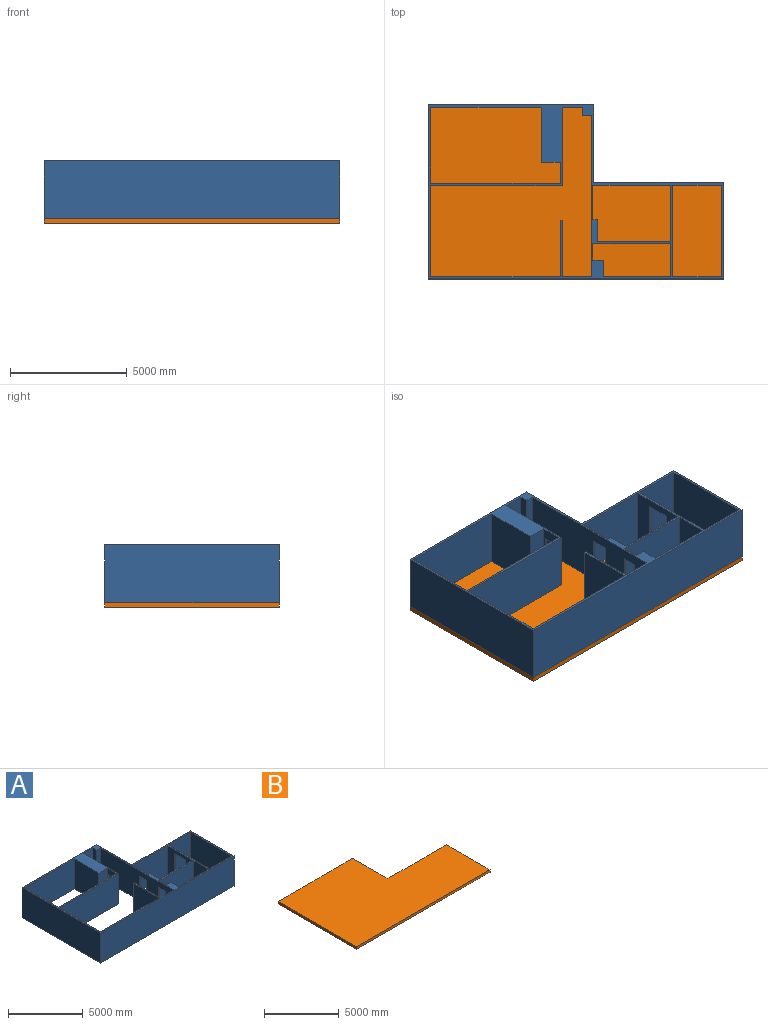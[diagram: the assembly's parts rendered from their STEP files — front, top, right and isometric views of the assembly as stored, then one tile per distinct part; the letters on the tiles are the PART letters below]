
ASSEMBLY  parts=2 mates=1
PART A: 54 faces, bbox 12650x7451.1x2470 mm
  f0: plane 12650x7451.1mm, normal (0,0,-1), area 8166293mm2, adj f1,f2,f3,f4,f5,f6,f7,f8
  f1: plane 2470x2420mm, normal (-1,0,0), area 3816000mm2, adj f0,f14,f15,f41,f48,f49,f50
  f2: plane 2470x1490mm, normal (1,0,0), area 2260300mm2, adj f0,f14,f35,f41,f45,f46,f47
  f3: plane 5630x2470mm, normal (0,-1,0), area 13906100mm2, adj f0,f4,f40,f41
  f4: plane 3351.1x2470mm, normal (1,0,0), area 6857217mm2, adj f0,f3,f5,f41,f51,f52,f53
  f5: plane 2470x890mm, normal (0,-1,0), area 2198300mm2, adj f0,f4,f6,f41
  f6: plane 2470x350mm, normal (-1,0,0), area 864500mm2, adj f0,f5,f7,f41
  f7: plane 2470x360mm, normal (0,-1,0), area 889200mm2, adj f0,f6,f8,f41
  f8: plane 6901.1x2470mm, normal (-1,0,0), area 14405717mm2, adj f0,f7,f9,f41,f42,f43,f44,f45
  f9: plane 2470x1250mm, normal (0,1,0), area 3087500mm2, adj f0,f8,f10,f41
  f10: plane 2470x2420mm, normal (1,0,0), area 5977400mm2, adj f0,f9,f11,f41
  f11: plane 2470x80mm, normal (0,1,0), area 197600mm2, adj f0,f10,f12,f41
  f12: plane 2470x2420mm, normal (-1,0,0), area 5977400mm2, adj f0,f11,f13,f41
  f13: plane 5550x2470mm, normal (0,1,0), area 13708500mm2, adj f0,f12,f40,f41
  f14: plane 3310x2470mm, normal (0,-1,0), area 8175700mm2, adj f0,f1,f2,f41
  f15: plane 3130x2470mm, normal (0,1,0), area 7731100mm2, adj f0,f1,f16,f41
  f16: plane 2470x930mm, normal (1,0,0), area 2297100mm2, adj f0,f15,f35,f41
  f17: plane 2470x901.1mm, normal (-1,0,0), area 805717mm2, adj f0,f18,f36,f41,f51,f52,f53
  f18: plane 5550x2470mm, normal (0,1,0), area 13708500mm2, adj f0,f17,f19,f41
  f19: plane 3251.1x2470mm, normal (1,0,0), area 8030217mm2, adj f0,f18,f20,f41
  f20: plane 4748.9x2470mm, normal (0,-1,0), area 11729783mm2, adj f0,f19,f21,f41
  f21: plane 2470x2350mm, normal (-1,0,0), area 5804500mm2, adj f0,f20,f36,f41
  f22: plane 7451.1x2470mm, normal (-1,0,0), area 18404217mm2, adj f0,f23,f37,f41
  f23: plane 12650x2470mm, normal (0,-1,0), area 31245500mm2, adj f0,f22,f24,f41
  f24: plane 4120x2470mm, normal (1,0,0), area 10176400mm2, adj f0,f23,f25,f41
  f25: plane 5570x2470mm, normal (0,1,0), area 13757900mm2, adj f0,f24,f26,f41
  f26: plane 3331.1x2470mm, normal (1,0,0), area 8227817mm2, adj f0,f25,f37,f41
  f27: plane 2470x1420mm, normal (-1,0,0), area 3507400mm2, adj f0,f28,f38,f41
  f28: plane 2870x2470mm, normal (0,1,0), area 7088900mm2, adj f0,f27,f29,f41
  f29: plane 2470x710mm, normal (1,0,0), area 1753700mm2, adj f0,f28,f30,f41
  f30: plane 2470x440mm, normal (0,1,0), area 1086800mm2, adj f0,f29,f31,f41
  f31: plane 2470x710mm, normal (1,0,0), area 533700mm2, adj f0,f30,f38,f41,f42,f43,f44
  f32: plane 3920x2470mm, normal (1,0,0), area 7521000mm2, adj f0,f33,f39,f41,f48,f49,f50
  f33: plane 2470x2090mm, normal (0,-1,0), area 5162300mm2, adj f0,f32,f34,f41
  f34: plane 3920x2470mm, normal (-1,0,0), area 9682400mm2, adj f0,f33,f39,f41
  f35: plane 2470x180mm, normal (0,1,0), area 444600mm2, adj f0,f2,f16,f41
  f36: plane 2470x801.1mm, normal (0,-1,0), area 1978717mm2, adj f0,f17,f21,f41
  f37: plane 7080x2470mm, normal (0,1,0), area 17487600mm2, adj f0,f22,f26,f41
  f38: plane 3310x2470mm, normal (0,-1,0), area 8175700mm2, adj f0,f27,f31,f41
  f39: plane 2470x2090mm, normal (0,1,0), area 5162300mm2, adj f0,f32,f34,f41
  f40: plane 3900x2470mm, normal (1,0,0), area 9633000mm2, adj f0,f3,f13,f41
  f41: plane 12650x7451.1mm, normal (0,0,1), area 8416493mm2, adj f1,f2,f3,f4,f5,f6,f7,f8
  f42: plane 2000x70mm, normal (0,1,0), area 140000mm2, adj f0,f8,f31,f44
  f43: plane 2000x70mm, normal (0,-1,0), area 140000mm2, adj f0,f8,f31,f44
  f44: plane 610x70mm, normal (0,0,-1), area 42700mm2, adj f8,f31,f42,f43
  f45: plane 2000x70mm, normal (0,1,0), area 140000mm2, adj f0,f2,f8,f47
  f46: plane 2000x70mm, normal (0,-1,0), area 140000mm2, adj f0,f2,f8,f47
  f47: plane 710x70mm, normal (0,0,-1), area 49700mm2, adj f2,f8,f45,f46
  f48: plane 2140x100mm, normal (0,-1,0), area 214000mm2, adj f0,f1,f32,f49
  f49: plane 1010x100mm, normal (0,0,-1), area 101000mm2, adj f1,f32,f48,f50
  f50: plane 2140x100mm, normal (0,1,0), area 214000mm2, adj f0,f1,f32,f49
  f51: plane 2000x80mm, normal (0,-1,0), area 160000mm2, adj f0,f4,f17,f53
  f52: plane 2000x80mm, normal (0,1,0), area 160000mm2, adj f0,f4,f17,f53
  f53: plane 710x80mm, normal (0,0,-1), area 56800mm2, adj f4,f17,f51,f52
PART B: 8 faces, bbox 12650x7451.1x200 mm
  f0: plane 7451.1x200mm, normal (-1,0,0), area 1490220mm2, adj f1,f5,f6,f7
  f1: plane 12650x200mm, normal (0,-1,0), area 2530000mm2, adj f0,f2,f6,f7
  f2: plane 4120x200mm, normal (1,0,0), area 824000mm2, adj f1,f3,f6,f7
  f3: plane 5570x200mm, normal (0,1,0), area 1114000mm2, adj f2,f4,f6,f7
  f4: plane 3331.1x200mm, normal (1,0,0), area 666220mm2, adj f3,f5,f6,f7
  f5: plane 7080x200mm, normal (0,1,0), area 1416000mm2, adj f0,f4,f6,f7
  f6: plane 12650x7451.1mm, normal (0,0,-1), area 75702188mm2, adj f0,f1,f2,f3,f4,f5
  f7: plane 12650x7451.1mm, normal (0,0,1), area 75702188mm2, adj f0,f1,f2,f3,f4,f5
PLACE A t=(242.64,9.35,200)mm
PLACE B t=(242.64,9.35,200)mm
MATE fastened A.f0 <-> B.f7  axis (0,0,-1) through (-5457.36,4230.45,200)mm
